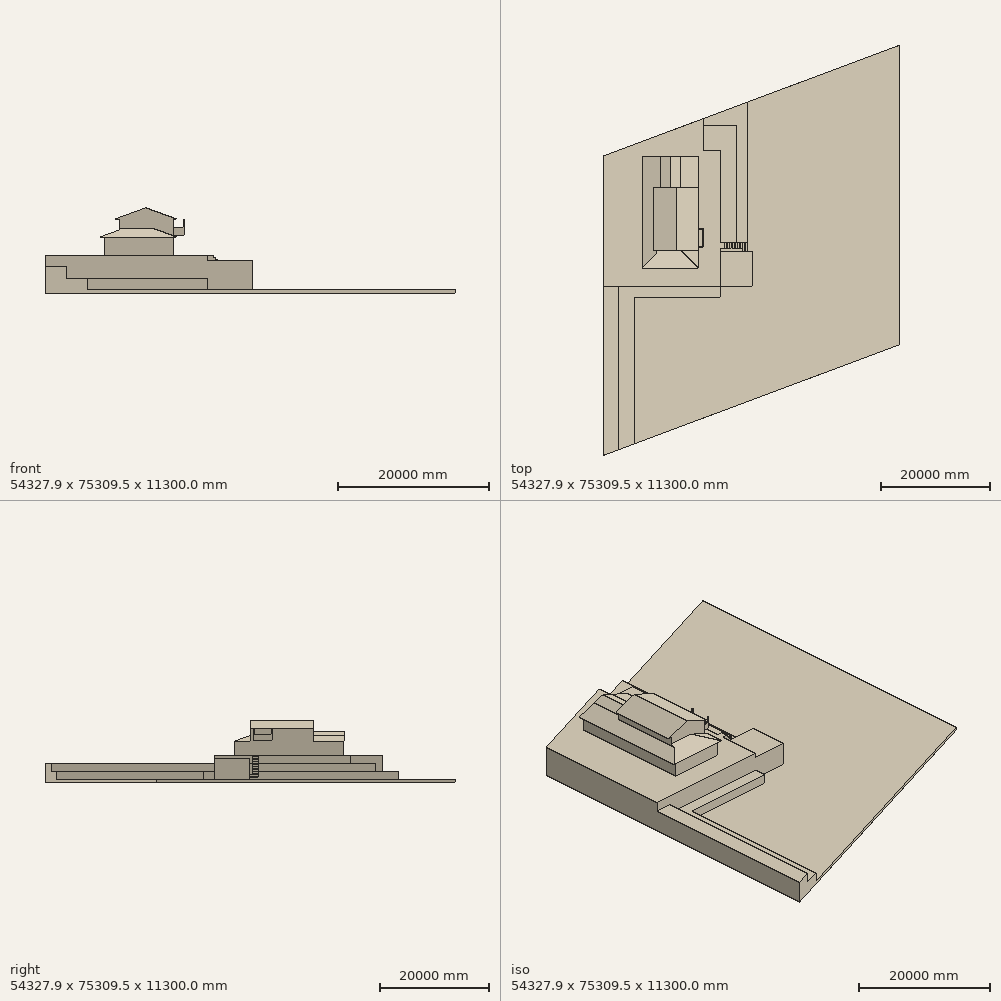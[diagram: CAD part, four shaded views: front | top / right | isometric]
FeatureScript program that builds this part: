
annotation { "Feature Type Name" : "Feature", "Feature Type Description" : "" }
export const myFeature = defineFeature(function(context is Context, id is Id, definition is map)
    precondition{}
    {
        {
            var Q0;
            Q0=qCreatedBy(makeId("Top.planeOp"),FACE);
            var sketch = newSketch(context, id + "F0", { "sketchPlane" : qUnion([Q0])});
            skLineSegment(sketch, "E0.bottom", {"start": v(0, 0) * mm, "end": v(-9140, 0) * mm});
            skLineSegment(sketch, "E0.top", {"start": v(0, 20000) * mm, "end": v(-9140, 20000) * mm});
            skLineSegment(sketch, "E0.left", {"start": v(0, 0) * mm, "end": v(0, 20000) * mm});
            skLineSegment(sketch, "E0.right", {"start": v(-9140, 0) * mm, "end": v(-9140, 20000) * mm});
            skSolve(sketch);
        }
        {
            var Q0;
            Q0=qSketchRegion(id+"F0",true);
            extrude(context, id + "F1", {"entities" : qUnion([Q0]), "depth" : 2400 * mm, "offsetDistance" : 25 * mm});
        }
        {
            var Q0;
            Q0=makeQuery(id+"F1.opExtrude","CAP_FACE",FACE,{"disambiguationData":[OSD([sQuery(id+"F0.wireOp",EDGE,"E0.bottom"),sQuery(id+"F0.wireOp",EDGE,"E0.top"),sQuery(id+"F0.wireOp",EDGE,"E0.left"),sQuery(id+"F0.wireOp",EDGE,"E0.right")])],"isStart":false});
            var sketch = newSketch(context, id + "F2", { "sketchPlane" : qUnion([Q0])});
            skLineSegment(sketch, "E1", {"start": v(0, 0) * mm, "end": v(0, 3000) * mm});
            skLineSegment(sketch, "E2", {"start": v(0, 3000) * mm, "end": v(-7140, 3000) * mm});
            skLineSegment(sketch, "E3", {"start": v(-7140, 3000) * mm, "end": v(-7140, 14500) * mm});
            skLineSegment(sketch, "E4", {"start": v(-7140, 14500) * mm, "end": v(0, 14500) * mm});
            skLineSegment(sketch, "E5", {"start": v(0, 14500) * mm, "end": v(0, 3000) * mm});
            skSolve(sketch);
        }
        {
            var Q0;
            Q0=qSketchRegion(id+"F2",true);
            extrude(context, id + "F3", {"entities" : qUnion([Q0]), "operationType" : NewBodyOperationType.ADD, "depth" : 2400 * mm, "offsetDistance" : 25 * mm});
        }
        {
            var Q0;
            Q0=makeQuery(id+"F3.opExtrude","CAP_FACE",FACE,{"disambiguationData":[OSD([sQuery(id+"F2.wireOp",EDGE,"E2"),sQuery(id+"F2.wireOp",EDGE,"E3"),sQuery(id+"F2.wireOp",EDGE,"E4"),sQuery(id+"F2.wireOp",EDGE,"E5")])],"isStart":false});
            var sketch = newSketch(context, id + "F4", { "sketchPlane" : qUnion([Q0])});
            skLineSegment(sketch, "E6", {"start": v(-3570, 3000) * mm, "end": v(-7740, 3000) * mm});
            skLineSegment(sketch, "E7", {"start": v(-7740, 3000) * mm, "end": v(-7740, 14500) * mm});
            skLineSegment(sketch, "E8", {"start": v(-7740, 14500) * mm, "end": v(600, 14500) * mm});
            skLineSegment(sketch, "E9", {"start": v(600, 14500) * mm, "end": v(600, 3000) * mm});
            skLineSegment(sketch, "E10", {"start": v(600, 3000) * mm, "end": v(-3570, 3000) * mm});
            skSolve(sketch);
        }
        {
            var Q0;
            Q0=qSketchRegion(id+"F4",true);
            extrude(context, id + "F5", {"entities" : qUnion([Q0]), "operationType" : NewBodyOperationType.ADD, "depth" : 1500 * mm, "offsetDistance" : 25 * mm});
        }
        {
            var Q0;
            Q0=makeQuery(id+"F5.opExtrude","CAP_EDGE",EDGE,{"disambiguationData":[OSD([sQuery(id+"F4.wireOp",EDGE,"E9")])],"isStart":false});
            var Q1;
            Q1=makeQuery(id+"F5.opExtrude","CAP_EDGE",EDGE,{"disambiguationData":[OSD([sQuery(id+"F4.wireOp",EDGE,"E7")])],"isStart":false});
            chamfer(context, id + "F6", {"entities" : qUnion([Q0, Q1]), "chamferType" : ChamferType.OFFSET_ANGLE, "width" : 4170 * mm, "oppositeDirection" : true, "angle" : 20 * degree, "tangentPropagation" : true});
        }
        {
            var Q0;
            Q0=makeQuery(id+"F1.opExtrude","CAP_FACE",FACE,{"disambiguationData":[OSD([sQuery(id+"F0.wireOp",EDGE,"E0.bottom"),sQuery(id+"F0.wireOp",EDGE,"E0.top"),sQuery(id+"F0.wireOp",EDGE,"E0.left"),sQuery(id+"F0.wireOp",EDGE,"E0.right")])],"isStart":false});
            var sketch = newSketch(context, id + "F7", { "sketchPlane" : qUnion([Q0])});
            skLineSegment(sketch, "E11", {"start": v(0, 3000) * mm, "end": v(-7140, 3000) * mm});
            skLineSegment(sketch, "E12", {"start": v(-9740, 3000) * mm, "end": v(-9740, -300) * mm});
            skLineSegment(sketch, "E13", {"start": v(-9740, -300) * mm, "end": v(600, -300) * mm});
            skLineSegment(sketch, "E14", {"start": v(600, -300) * mm, "end": v(600, 3000) * mm});
            skLineSegment(sketch, "E15", {"start": v(600, 3000) * mm, "end": v(0, 3000) * mm});
            skPoint(sketch, "E16.start.orphan", {"position": v(600, 14500) * mm});
            skLineSegment(sketch, "E17", {"start": v(-7140, 3000) * mm, "end": v(-7140, 14500) * mm});
            skLineSegment(sketch, "E18", {"start": v(-7140, 14500) * mm, "end": v(600, 14500) * mm});
            skLineSegment(sketch, "E19", {"start": v(600, 14500) * mm, "end": v(600, 20300) * mm});
            skLineSegment(sketch, "E20", {"start": v(600, 20300) * mm, "end": v(-9740, 20300) * mm});
            skLineSegment(sketch, "E21", {"start": v(-9740, 20300) * mm, "end": v(-9740, 3000) * mm});
            skSolve(sketch);
        }
        {
            var Q0;
            Q0=qSketchRegion(id+"F7",true);
            extrude(context, id + "F8", {"entities" : qUnion([Q0]), "operationType" : NewBodyOperationType.ADD, "depth" : 1200 * mm, "offsetDistance" : 25 * mm});
        }
        {
            var Q0;
            Q0=makeQuery(id+"F8.opExtrude","CAP_EDGE",EDGE,{"disambiguationData":[OSD([sQuery(id+"F7.wireOp",EDGE,"E13")])],"isStart":false});
            var Q1;
            Q1=makeQuery(id+"F8.opExtrude","CAP_EDGE",EDGE,{"disambiguationData":[OSD([sQuery(id+"F7.wireOp",EDGE,"E14")])],"isStart":false});
            chamfer(context, id + "F9", {"entities" : qUnion([Q0, Q1]), "chamferType" : ChamferType.OFFSET_ANGLE, "width" : 3300 * mm, "oppositeDirection" : false, "angle" : 20 * degree, "tangentPropagation" : true});
        }
        {
            var Q0;
            Q0=makeQuery(id+"F8.opExtrude","CAP_EDGE",EDGE,{"disambiguationData":[OSD([sQuery(id+"F7.wireOp",EDGE,"E19")])],"isStart":false});
            var Q1;
            Q1=makeQuery(id+"F8.opExtrude","CAP_EDGE",EDGE,{"disambiguationData":[OSD([sQuery(id+"F7.wireOp",EDGE,"E12"),sQuery(id+"F7.wireOp",EDGE,"E21")])],"isStart":false});
            chamfer(context, id + "F10", {"entities" : qUnion([Q0, Q1]), "chamferType" : ChamferType.OFFSET_ANGLE, "width" : 3300 * mm, "oppositeDirection" : false, "angle" : 20 * degree, "tangentPropagation" : true});
        }
        {
            var Q0;
            Q0=makeQuery(id+"F8.opExtrude","CAP_FACE",FACE,{"disambiguationData":[OSD([sQuery(id+"F7.wireOp",EDGE,"E11"),sQuery(id+"F7.wireOp",EDGE,"E12"),sQuery(id+"F7.wireOp",EDGE,"E13"),sQuery(id+"F7.wireOp",EDGE,"E14"),sQuery(id+"F7.wireOp",EDGE,"E15"),sQuery(id+"F7.wireOp",EDGE,"E17"),sQuery(id+"F7.wireOp",EDGE,"E18"),sQuery(id+"F7.wireOp",EDGE,"E19"),sQuery(id+"F7.wireOp",EDGE,"E20"),sQuery(id+"F7.wireOp",EDGE,"E21")])],"isStart":false});
            extrude(context, id + "F11", {"entities" : qUnion([Q0]), "operationType" : NewBodyOperationType.ADD, "depth" : 700 * mm, "offsetDistance" : 25 * mm});
        }
        {
            var Q0;
            {var subQ0=sQuery(id+"F7.wireOp",EDGE,"E21");var subQ1=sQuery(id+"F7.wireOp",EDGE,"E20");var subQ2=sQuery(id+"F7.wireOp",EDGE,"E19");var subQ3=sQuery(id+"F7.wireOp",EDGE,"E18");var subQ4=sQuery(id+"F7.wireOp",EDGE,"E17");var subQ5=sQuery(id+"F7.wireOp",EDGE,"E15");var subQ6=sQuery(id+"F7.wireOp",EDGE,"E14");var subQ7=sQuery(id+"F7.wireOp",EDGE,"E13");var subQ8=sQuery(id+"F7.wireOp",EDGE,"E12");var subQ9=sQuery(id+"F7.wireOp",EDGE,"E11");Q0=makeQuery(id+"F11.opExtrude","CAP_EDGE",EDGE,{"disambiguationData":[OSD([subQ9,subQ8,subQ7,subQ6,subQ5,subQ4,subQ3,subQ2,subQ1,subQ0]),TDD([makeQuery(id+"F10.opChamfer","BLEND_EDGE",EDGE,{"blendedFrom":[makeQuery(id+"F8.opExtrude","CAP_EDGE",EDGE,{"disambiguationData":[OSD([subQ8,subQ0])],"isStart":false}),makeQuery(id+"F8.opExtrude","CAP_FACE",FACE,{"disambiguationData":[OSD([subQ9,subQ8,subQ7,subQ6,subQ5,subQ4,subQ3,subQ2,subQ1,subQ0])],"isStart":false})],"blendedInto":[makeQuery(id+"F8.opExtrude","CAP_FACE",FACE,{"disambiguationData":[OSD([subQ9,subQ8,subQ7,subQ6,subQ5,subQ4,subQ3,subQ2,subQ1,subQ0])],"isStart":false})]})])],"isStart":false});}
            var Q1;
            {var subQ0=sQuery(id+"F7.wireOp",EDGE,"E21");var subQ1=sQuery(id+"F7.wireOp",EDGE,"E20");var subQ2=sQuery(id+"F7.wireOp",EDGE,"E19");var subQ3=sQuery(id+"F7.wireOp",EDGE,"E18");var subQ4=sQuery(id+"F7.wireOp",EDGE,"E17");var subQ5=sQuery(id+"F7.wireOp",EDGE,"E15");var subQ6=sQuery(id+"F7.wireOp",EDGE,"E14");var subQ7=sQuery(id+"F7.wireOp",EDGE,"E13");var subQ8=sQuery(id+"F7.wireOp",EDGE,"E12");var subQ9=sQuery(id+"F7.wireOp",EDGE,"E11");Q1=makeQuery(id+"F11.opExtrude","CAP_EDGE",EDGE,{"disambiguationData":[OSD([subQ9,subQ8,subQ7,subQ6,subQ5,subQ4,subQ3,subQ2,subQ1,subQ0]),TDD([makeQuery(id+"F10.opChamfer","BLEND_EDGE",EDGE,{"blendedFrom":[makeQuery(id+"F8.opExtrude","CAP_EDGE",EDGE,{"disambiguationData":[OSD([subQ2])],"isStart":false}),makeQuery(id+"F8.opExtrude","CAP_FACE",FACE,{"disambiguationData":[OSD([subQ9,subQ8,subQ7,subQ6,subQ5,subQ4,subQ3,subQ2,subQ1,subQ0])],"isStart":false})],"blendedInto":[makeQuery(id+"F8.opExtrude","CAP_FACE",FACE,{"disambiguationData":[OSD([subQ9,subQ8,subQ7,subQ6,subQ5,subQ4,subQ3,subQ2,subQ1,subQ0])],"isStart":false})]})])],"isStart":false});}
            chamfer(context, id + "F12", {"entities" : qUnion([Q0, Q1]), "chamferType" : ChamferType.OFFSET_ANGLE, "width" : 1923.2 * mm, "oppositeDirection" : false, "angle" : 20 * degree, "tangentPropagation" : true});
        }
        {
            var Q0;
            Q0=makeQuery(id+"F1.opExtrude","CAP_FACE",FACE,{"disambiguationData":[OSD([sQuery(id+"F0.wireOp",EDGE,"E0.bottom"),sQuery(id+"F0.wireOp",EDGE,"E0.top"),sQuery(id+"F0.wireOp",EDGE,"E0.left"),sQuery(id+"F0.wireOp",EDGE,"E0.right")])],"isStart":true});
            var sketch = newSketch(context, id + "F13", { "sketchPlane" : qUnion([Q0])});
            skLineSegment(sketch, "E22", {"start": v(0, 0) * mm, "end": v(0, 3700) * mm});
            skLineSegment(sketch, "E23", {"start": v(0, 3700) * mm, "end": v(4500, 3700) * mm});
            skLineSegment(sketch, "E24", {"start": v(4500, 3700) * mm, "end": v(4500, -28300) * mm});
            skLineSegment(sketch, "E25", {"start": v(0, 3700) * mm, "end": v(-16900, 3700) * mm});
            skLineSegment(sketch, "E26", {"start": v(-16900, 3700) * mm, "end": v(-16900, -20300) * mm});
            skLineSegment(sketch, "E27", {"start": v(-16900, -20300) * mm, "end": v(4500, -28300) * mm});
            skSolve(sketch);
        }
        {
            var Q0;
            Q0=qSketchRegion(id+"F13",true);
            extrude(context, id + "F14", {"entities" : qUnion([Q0]), "operationType" : NewBodyOperationType.ADD, "depth" : 200 * mm, "offsetDistance" : 25 * mm});
        }
        {
            var Q0;
            Q0=makeQuery(id+"F14.opExtrude","CAP_FACE",FACE,{"disambiguationData":[OSD([sQuery(id+"F13.wireOp",EDGE,"E23"),sQuery(id+"F13.wireOp",EDGE,"E24"),sQuery(id+"F13.wireOp",EDGE,"E25"),sQuery(id+"F13.wireOp",EDGE,"E26"),sQuery(id+"F13.wireOp",EDGE,"E27")])],"isStart":false});
            var sketch = newSketch(context, id + "F15", { "sketchPlane" : qUnion([Q0])});
            skLineSegment(sketch, "E28", {"start": v(-16900, -20300) * mm, "end": v(37427.93, -40609.5) * mm});
            skLineSegment(sketch, "E29", {"start": v(37427.93, -40609.5) * mm, "end": v(37427.93, 14390.5) * mm});
            skLineSegment(sketch, "E30", {"start": v(37427.93, 14390.5) * mm, "end": v(-16900, 34700) * mm});
            skLineSegment(sketch, "E31", {"start": v(-16900, 34700) * mm, "end": v(-16900, -20300) * mm});
            skSolve(sketch);
        }
        {
            var Q0;
            Q0=qSketchRegion(id+"F15",true);
            extrude(context, id + "F16", {"entities" : qUnion([Q0]), "operationType" : NewBodyOperationType.ADD, "depth" : 4800 * mm, "offsetDistance" : 25 * mm});
        }
        {
            var Q0;
            Q0=makeQuery(id+"F16.opExtrude","CAP_FACE",FACE,{"disambiguationData":[OSD([sQuery(id+"F15.wireOp",EDGE,"E28"),sQuery(id+"F15.wireOp",EDGE,"E29"),sQuery(id+"F15.wireOp",EDGE,"E30"),sQuery(id+"F15.wireOp",EDGE,"E31")])],"isStart":true});
            extrude(context, id + "F17", {"entities" : qUnion([Q0]), "operationType" : NewBodyOperationType.ADD, "depth" : 25 * mm, "offsetDistance" : 25 * mm});
        }
        {
            var Q0;
            Q0=makeQuery(id+"F17.opExtrude","CAP_FACE",FACE,{"disambiguationData":[OSD([sQuery(id+"F15.wireOp",EDGE,"E28"),sQuery(id+"F15.wireOp",EDGE,"E29"),sQuery(id+"F15.wireOp",EDGE,"E30"),sQuery(id+"F15.wireOp",EDGE,"E31")])],"isStart":false});
            var sketch = newSketch(context, id + "F18", { "sketchPlane" : qUnion([Q0])});
            skLineSegment(sketch, "E32", {"start": v(-16900, -3700) * mm, "end": v(4500, -3700) * mm});
            skLineSegment(sketch, "E33", {"start": v(4500, -3700) * mm, "end": v(4500, 28300) * mm});
            skLineSegment(sketch, "E34", {"start": v(4500, 28300) * mm, "end": v(37427.93, 40609.5) * mm});
            skLineSegment(sketch, "E35", {"start": v(37427.93, 40609.5) * mm, "end": v(37427.93, -14390.5) * mm});
            skLineSegment(sketch, "E36", {"start": v(37427.93, -14390.5) * mm, "end": v(-16900, -34700) * mm});
            skLineSegment(sketch, "E37", {"start": v(-16900, -34700) * mm, "end": v(-16900, -3700) * mm});
            skSolve(sketch);
        }
        {
            var Q0;
            Q0=qSketchRegion(id+"F18",true);
            extrude(context, id + "F19", {"entities" : qUnion([Q0]), "operationType" : NewBodyOperationType.REMOVE, "oppositeDirection" : true, "depth" : 1325 * mm, "offsetDistance" : 25 * mm});
        }
        {
            var Q0;
            Q0=makeQuery(id+"F14.opExtrude","CAP_FACE",FACE,{"disambiguationData":[OSD([sQuery(id+"F13.wireOp",EDGE,"E23"),sQuery(id+"F13.wireOp",EDGE,"E24"),sQuery(id+"F13.wireOp",EDGE,"E25"),sQuery(id+"F13.wireOp",EDGE,"E26"),sQuery(id+"F13.wireOp",EDGE,"E27")])],"isStart":true});
            var sketch = newSketch(context, id + "F20", { "sketchPlane" : qUnion([Q0])});
            skLineSegment(sketch, "E38", {"start": v(4500, 28300) * mm, "end": v(4500, 21300) * mm});
            skLineSegment(sketch, "E39", {"start": v(4500, 21300) * mm, "end": v(1500, 21300) * mm});
            skLineSegment(sketch, "E40", {"start": v(1500, 21300) * mm, "end": v(1500, 27178.5) * mm});
            skLineSegment(sketch, "E41", {"start": v(1500, 27178.5) * mm, "end": v(4500, 28300) * mm});
            skSolve(sketch);
        }
        {
            var Q0;
            Q0=qSketchRegion(id+"F20",true);
            extrude(context, id + "F21", {"entities" : qUnion([Q0]), "operationType" : NewBodyOperationType.REMOVE, "oppositeDirection" : true, "depth" : 1500 * mm, "offsetDistance" : 25 * mm});
        }
        {
            var Q0;
            Q0=makeQuery(id+"F21.boolean.opBoolean","MERGE",FACE,{"derivedFrom":[makeQuery(id+"F19.boolean.opBoolean","COPY",FACE,{"derivedFrom":makeQuery(id+"F19.opExtrude","CAP_FACE",FACE,{"disambiguationData":[OSD([sQuery(id+"F18.wireOp",EDGE,"E32"),sQuery(id+"F18.wireOp",EDGE,"E33"),sQuery(id+"F18.wireOp",EDGE,"E34"),sQuery(id+"F18.wireOp",EDGE,"E35"),sQuery(id+"F18.wireOp",EDGE,"E36"),sQuery(id+"F18.wireOp",EDGE,"E37")])],"isStart":false})})],"fromTools":[makeQuery(id+"F21.opExtrude","CAP_FACE",FACE,{"disambiguationData":[OSD([sQuery(id+"F20.wireOp",EDGE,"E38"),sQuery(id+"F20.wireOp",EDGE,"E39"),sQuery(id+"F20.wireOp",EDGE,"E40"),sQuery(id+"F20.wireOp",EDGE,"E41")])],"isStart":false})]});
            var sketch = newSketch(context, id + "F22", { "sketchPlane" : qUnion([Q0])});
            skLineSegment(sketch, "E42", {"start": v(4500, -3700) * mm, "end": v(4500, 4440) * mm});
            skLineSegment(sketch, "E43", {"start": v(4500, 4440) * mm, "end": v(7500, 4440) * mm});
            skLineSegment(sketch, "E44", {"start": v(7500, 4440) * mm, "end": v(7500, 25900) * mm});
            skLineSegment(sketch, "E45", {"start": v(7500, 25900) * mm, "end": v(1500, 25900) * mm});
            skLineSegment(sketch, "E46", {"start": v(1500, 25900) * mm, "end": v(1500, 27178.5) * mm});
            skLineSegment(sketch, "E47", {"start": v(1500, 27178.5) * mm, "end": v(37427.93, 40609.5) * mm});
            skLineSegment(sketch, "E48", {"start": v(37427.93, 40609.5) * mm, "end": v(37427.93, -14390.5) * mm});
            skLineSegment(sketch, "E49", {"start": v(37427.93, -14390.5) * mm, "end": v(-14089.93, -33649.5) * mm});
            skLineSegment(sketch, "E50", {"start": v(-14089.93, -33649.5) * mm, "end": v(-14089.93, -3700) * mm});
            skLineSegment(sketch, "E51", {"start": v(-14089.93, -3700) * mm, "end": v(4500, -3700) * mm});
            skSolve(sketch);
        }
        {
            var Q0;
            Q0=qSketchRegion(id+"F22",true);
            extrude(context, id + "F23", {"entities" : qUnion([Q0]), "operationType" : NewBodyOperationType.REMOVE, "oppositeDirection" : true, "depth" : 1500 * mm, "offsetDistance" : 25 * mm});
        }
        {
            var Q0;
            Q0=makeQuery(id+"F23.boolean.opBoolean","COPY",FACE,{"derivedFrom":makeQuery(id+"F23.opExtrude","CAP_FACE",FACE,{"disambiguationData":[OSD([sQuery(id+"F22.wireOp",EDGE,"E42"),sQuery(id+"F22.wireOp",EDGE,"E43"),sQuery(id+"F22.wireOp",EDGE,"E44"),sQuery(id+"F22.wireOp",EDGE,"E45"),sQuery(id+"F22.wireOp",EDGE,"E46"),sQuery(id+"F22.wireOp",EDGE,"E47"),sQuery(id+"F22.wireOp",EDGE,"E48"),sQuery(id+"F22.wireOp",EDGE,"E49"),sQuery(id+"F22.wireOp",EDGE,"E50"),sQuery(id+"F22.wireOp",EDGE,"E51")])],"isStart":false})});
            var sketch = newSketch(context, id + "F24", { "sketchPlane" : qUnion([Q0])});
            skLineSegment(sketch, "E52", {"start": v(4500, -3700) * mm, "end": v(4500, 4440) * mm});
            skLineSegment(sketch, "E53", {"start": v(4500, 4440) * mm, "end": v(9500, 4440) * mm});
            skLineSegment(sketch, "E54", {"start": v(9500, 4440) * mm, "end": v(9500, 30169.16) * mm});
            skLineSegment(sketch, "E55", {"start": v(9500, 30169.16) * mm, "end": v(37427.93, 40609.5) * mm});
            skLineSegment(sketch, "E56", {"start": v(37427.93, 40609.5) * mm, "end": v(37427.93, -14390.5) * mm});
            skLineSegment(sketch, "E57", {"start": v(37427.93, -14390.5) * mm, "end": v(-11279.87, -32599.02) * mm});
            skLineSegment(sketch, "E58", {"start": v(-11279.87, -32599.02) * mm, "end": v(-11279.87, -5700) * mm});
            skLineSegment(sketch, "E59", {"start": v(-11279.87, -5700) * mm, "end": v(4500, -5700) * mm});
            skLineSegment(sketch, "E60", {"start": v(4500, -5700) * mm, "end": v(4500, -3700) * mm});
            skSolve(sketch);
        }
        {
            var Q0;
            Q0=qSketchRegion(id+"F24",true);
            extrude(context, id + "F25", {"entities" : qUnion([Q0]), "operationType" : NewBodyOperationType.REMOVE, "oppositeDirection" : true, "depth" : 1500 * mm, "offsetDistance" : 25 * mm});
        }
        {
            var Q0;
            Q0=makeQuery(id+"F25.boolean.opBoolean","COPY",FACE,{"derivedFrom":makeQuery(id+"F25.opExtrude","CAP_FACE",FACE,{"disambiguationData":[OSD([sQuery(id+"F24.wireOp",EDGE,"E52"),sQuery(id+"F24.wireOp",EDGE,"E53"),sQuery(id+"F24.wireOp",EDGE,"E54"),sQuery(id+"F24.wireOp",EDGE,"E55"),sQuery(id+"F24.wireOp",EDGE,"E56"),sQuery(id+"F24.wireOp",EDGE,"E57"),sQuery(id+"F24.wireOp",EDGE,"E58"),sQuery(id+"F24.wireOp",EDGE,"E59"),sQuery(id+"F24.wireOp",EDGE,"E60")])],"isStart":false})});
            var sketch = newSketch(context, id + "F26", { "sketchPlane" : qUnion([Q0])});
            skLineSegment(sketch, "E61", {"start": v(4500, -3700) * mm, "end": v(4500, 3300) * mm});
            skLineSegment(sketch, "E62", {"start": v(4500, 3300) * mm, "end": v(10500, 3300) * mm});
            skLineSegment(sketch, "E63", {"start": v(10500, 3300) * mm, "end": v(10500, -3700) * mm});
            skLineSegment(sketch, "E64", {"start": v(10500, -3700) * mm, "end": v(4500, -3700) * mm});
            skSolve(sketch);
        }
        {
            var Q0;
            Q0=qSketchRegion(id+"F26",true);
            extrude(context, id + "F27", {"entities" : qUnion([Q0]), "operationType" : NewBodyOperationType.ADD, "depth" : 3800 * mm, "offsetDistance" : 25 * mm});
        }
        {
            var Q0;
            Q0=makeQuery(id+"F25.boolean.opBoolean","COPY",FACE,{"derivedFrom":makeQuery(id+"F25.opExtrude","CAP_FACE",FACE,{"disambiguationData":[OSD([sQuery(id+"F24.wireOp",EDGE,"E52"),sQuery(id+"F24.wireOp",EDGE,"E53"),sQuery(id+"F24.wireOp",EDGE,"E54"),sQuery(id+"F24.wireOp",EDGE,"E55"),sQuery(id+"F24.wireOp",EDGE,"E56"),sQuery(id+"F24.wireOp",EDGE,"E57"),sQuery(id+"F24.wireOp",EDGE,"E58"),sQuery(id+"F24.wireOp",EDGE,"E59"),sQuery(id+"F24.wireOp",EDGE,"E60")])],"isStart":false})});
            var sketch = newSketch(context, id + "F28", { "sketchPlane" : qUnion([Q0])});
            skLineSegment(sketch, "E65", {"start": v(9500, 4440) * mm, "end": v(9500, 3300) * mm});
            skLineSegment(sketch, "E66", {"start": v(9500, 3300) * mm, "end": v(4500, 3300) * mm});
            skLineSegment(sketch, "E67", {"start": v(4500, 3300) * mm, "end": v(4500, 4440) * mm});
            skLineSegment(sketch, "E68", {"start": v(4500, 4440) * mm, "end": v(9500, 4440) * mm});
            skSolve(sketch);
        }
        {
            var Q0;
            Q0=qSketchRegion(id+"F28",true);
            extrude(context, id + "F29", {"entities" : qUnion([Q0]), "operationType" : NewBodyOperationType.ADD, "depth" : 300 * mm, "offsetDistance" : 25 * mm});
        }
        {
            var Q0;
            Q0=makeQuery(id+"F29.opExtrude","CAP_FACE",FACE,{"disambiguationData":[OSD([sQuery(id+"F28.wireOp",EDGE,"E65"),sQuery(id+"F28.wireOp",EDGE,"E66"),sQuery(id+"F28.wireOp",EDGE,"E67"),sQuery(id+"F28.wireOp",EDGE,"E68")])],"isStart":false});
            var sketch = newSketch(context, id + "F30", { "sketchPlane" : qUnion([Q0])});
            skLineSegment(sketch, "E69", {"start": v(4500, 4440) * mm, "end": v(9200, 4440) * mm});
            skLineSegment(sketch, "E70", {"start": v(9200, 4440) * mm, "end": v(9200, 3300) * mm});
            skLineSegment(sketch, "E71", {"start": v(9200, 3300) * mm, "end": v(4500, 3300) * mm});
            skLineSegment(sketch, "E72", {"start": v(4500, 3300) * mm, "end": v(4500, 4351.93) * mm});
            skLineSegment(sketch, "E73", {"start": v(4500, 4351.93) * mm, "end": v(4500, 4440) * mm});
            skSolve(sketch);
        }
        {
            var Q0;
            Q0=qSketchRegion(id+"F30",true);
            extrude(context, id + "F31", {"entities" : qUnion([Q0]), "operationType" : NewBodyOperationType.ADD, "depth" : 300 * mm, "offsetDistance" : 25 * mm});
        }
        {
            var Q0;
            Q0=makeQuery(id+"F31.opExtrude","CAP_FACE",FACE,{"disambiguationData":[OSD([sQuery(id+"F30.wireOp",EDGE,"E69"),sQuery(id+"F30.wireOp",EDGE,"E70"),sQuery(id+"F30.wireOp",EDGE,"E71"),sQuery(id+"F30.wireOp",EDGE,"E72"),sQuery(id+"F30.wireOp",EDGE,"E73")])],"isStart":false});
            var sketch = newSketch(context, id + "F32", { "sketchPlane" : qUnion([Q0])});
            skLineSegment(sketch, "E74.bottom", {"start": v(4500, 4440) * mm, "end": v(8900, 4440) * mm});
            skLineSegment(sketch, "E74.top", {"start": v(4500, 3300) * mm, "end": v(8900, 3300) * mm});
            skLineSegment(sketch, "E74.left", {"start": v(4500, 4440) * mm, "end": v(4500, 3300) * mm});
            skLineSegment(sketch, "E74.right", {"start": v(8900, 4440) * mm, "end": v(8900, 3300) * mm});
            skSolve(sketch);
        }
        {
            var Q0;
            Q0=qSketchRegion(id+"F32",true);
            extrude(context, id + "F33", {"entities" : qUnion([Q0]), "operationType" : NewBodyOperationType.ADD, "depth" : 300 * mm, "offsetDistance" : 25 * mm});
        }
        {
            var Q0;
            Q0=makeQuery(id+"F33.opExtrude","CAP_FACE",FACE,{"disambiguationData":[OSD([sQuery(id+"F32.wireOp",EDGE,"E74.bottom"),sQuery(id+"F32.wireOp",EDGE,"E74.top"),sQuery(id+"F32.wireOp",EDGE,"E74.left"),sQuery(id+"F32.wireOp",EDGE,"E74.right")])],"isStart":false});
            var sketch = newSketch(context, id + "F34", { "sketchPlane" : qUnion([Q0])});
            skLineSegment(sketch, "E75.bottom", {"start": v(4500, 4440) * mm, "end": v(8600, 4440) * mm});
            skLineSegment(sketch, "E75.top", {"start": v(4500, 3300) * mm, "end": v(8600, 3300) * mm});
            skLineSegment(sketch, "E75.left", {"start": v(4500, 4440) * mm, "end": v(4500, 3300) * mm});
            skLineSegment(sketch, "E75.right", {"start": v(8600, 4440) * mm, "end": v(8600, 3300) * mm});
            skSolve(sketch);
        }
        {
            var Q0;
            Q0=qSketchRegion(id+"F34",true);
            extrude(context, id + "F35", {"entities" : qUnion([Q0]), "operationType" : NewBodyOperationType.ADD, "depth" : 300 * mm, "offsetDistance" : 25 * mm});
        }
        {
            var Q0;
            Q0=makeQuery(id+"F35.opExtrude","CAP_FACE",FACE,{"disambiguationData":[OSD([sQuery(id+"F34.wireOp",EDGE,"E75.bottom"),sQuery(id+"F34.wireOp",EDGE,"E75.top"),sQuery(id+"F34.wireOp",EDGE,"E75.left"),sQuery(id+"F34.wireOp",EDGE,"E75.right")])],"isStart":false});
            var sketch = newSketch(context, id + "F36", { "sketchPlane" : qUnion([Q0])});
            skLineSegment(sketch, "E76.bottom", {"start": v(4500, 4440) * mm, "end": v(8300, 4440) * mm});
            skLineSegment(sketch, "E76.top", {"start": v(4500, 3300) * mm, "end": v(8300, 3300) * mm});
            skLineSegment(sketch, "E76.left", {"start": v(4500, 4440) * mm, "end": v(4500, 3300) * mm});
            skLineSegment(sketch, "E76.right", {"start": v(8300, 4440) * mm, "end": v(8300, 3300) * mm});
            skSolve(sketch);
        }
        {
            var Q0;
            Q0=qSketchRegion(id+"F36",true);
            extrude(context, id + "F37", {"entities" : qUnion([Q0]), "operationType" : NewBodyOperationType.ADD, "depth" : 300 * mm, "offsetDistance" : 25 * mm});
        }
        {
            var Q0;
            {var subQ1=sQuery(id+"F22.wireOp",EDGE,"E45");var subQ2=sQuery(id+"F22.wireOp",EDGE,"E43");var subQ3=sQuery(id+"F22.wireOp",EDGE,"E44");Q0=makeQuery(id+"F37.boolean.opBoolean","MERGE",FACE,{"derivedFrom":[makeQuery(id+"F25.boolean.opBoolean","SPLIT",FACE,{"disambiguationData":[TD([makeQuery(id+"F14.opExtrude","SWEPT_FACE",FACE,{"disambiguationData":[OSD([sQuery(id+"F13.wireOp",EDGE,"E27")])]})])],"derivedFrom":makeQuery(id+"F23.boolean.opBoolean","COPY",FACE,{"derivedFrom":makeQuery(id+"F23.opExtrude","CAP_FACE",FACE,{"disambiguationData":[OSD([sQuery(id+"F22.wireOp",EDGE,"E42"),subQ2,subQ3,subQ1,sQuery(id+"F22.wireOp",EDGE,"E46"),sQuery(id+"F22.wireOp",EDGE,"E47"),sQuery(id+"F22.wireOp",EDGE,"E48"),sQuery(id+"F22.wireOp",EDGE,"E49"),sQuery(id+"F22.wireOp",EDGE,"E50"),sQuery(id+"F22.wireOp",EDGE,"E51")])],"isStart":false})})}),makeQuery(id+"F37.opExtrude","CAP_FACE",FACE,{"disambiguationData":[OSD([sQuery(id+"F36.wireOp",EDGE,"E76.bottom"),sQuery(id+"F36.wireOp",EDGE,"E76.top"),sQuery(id+"F36.wireOp",EDGE,"E76.left"),sQuery(id+"F36.wireOp",EDGE,"E76.right")])],"isStart":false})]});}
            var sketch = newSketch(context, id + "F38", { "sketchPlane" : qUnion([Q0])});
            skLineSegment(sketch, "E77.bottom", {"start": v(4500, 4440) * mm, "end": v(8000, 4440) * mm});
            skLineSegment(sketch, "E77.top", {"start": v(4500, 3300) * mm, "end": v(8000, 3300) * mm});
            skLineSegment(sketch, "E77.left", {"start": v(4500, 4440) * mm, "end": v(4500, 3300) * mm});
            skLineSegment(sketch, "E77.right", {"start": v(8000, 4440) * mm, "end": v(8000, 3300) * mm});
            skSolve(sketch);
        }
        {
            var Q0;
            Q0=qSketchRegion(id+"F38",true);
            extrude(context, id + "F39", {"entities" : qUnion([Q0]), "operationType" : NewBodyOperationType.ADD, "depth" : 300 * mm, "offsetDistance" : 25 * mm});
        }
        {
            var Q0;
            Q0=makeQuery(id+"F39.opExtrude","CAP_FACE",FACE,{"disambiguationData":[OSD([sQuery(id+"F38.wireOp",EDGE,"E77.bottom"),sQuery(id+"F38.wireOp",EDGE,"E77.top"),sQuery(id+"F38.wireOp",EDGE,"E77.left"),sQuery(id+"F38.wireOp",EDGE,"E77.right")])],"isStart":false});
            var sketch = newSketch(context, id + "F40", { "sketchPlane" : qUnion([Q0])});
            skLineSegment(sketch, "E78.bottom", {"start": v(4500, 4440) * mm, "end": v(7700, 4440) * mm});
            skLineSegment(sketch, "E78.top", {"start": v(4500, 3300) * mm, "end": v(7700, 3300) * mm});
            skLineSegment(sketch, "E78.left", {"start": v(4500, 4440) * mm, "end": v(4500, 3300) * mm});
            skLineSegment(sketch, "E78.right", {"start": v(7700, 4440) * mm, "end": v(7700, 3300) * mm});
            skSolve(sketch);
        }
        {
            var Q0;
            Q0=qSketchRegion(id+"F40",true);
            extrude(context, id + "F41", {"entities" : qUnion([Q0]), "operationType" : NewBodyOperationType.ADD, "depth" : 300 * mm, "offsetDistance" : 25 * mm});
        }
        {
            var Q0;
            Q0=makeQuery(id+"F41.opExtrude","CAP_FACE",FACE,{"disambiguationData":[OSD([sQuery(id+"F40.wireOp",EDGE,"E78.bottom"),sQuery(id+"F40.wireOp",EDGE,"E78.top"),sQuery(id+"F40.wireOp",EDGE,"E78.left"),sQuery(id+"F40.wireOp",EDGE,"E78.right")])],"isStart":false});
            var sketch = newSketch(context, id + "F42", { "sketchPlane" : qUnion([Q0])});
            skLineSegment(sketch, "E79.bottom", {"start": v(4500, 4440) * mm, "end": v(7400, 4440) * mm});
            skLineSegment(sketch, "E79.top", {"start": v(4500, 3300) * mm, "end": v(7400, 3300) * mm});
            skLineSegment(sketch, "E79.left", {"start": v(4500, 4440) * mm, "end": v(4500, 3300) * mm});
            skLineSegment(sketch, "E79.right", {"start": v(7400, 4440) * mm, "end": v(7400, 3300) * mm});
            skSolve(sketch);
        }
        {
            var Q0;
            Q0=qSketchRegion(id+"F42",true);
            extrude(context, id + "F43", {"entities" : qUnion([Q0]), "operationType" : NewBodyOperationType.ADD, "depth" : 300 * mm, "offsetDistance" : 25 * mm});
        }
        {
            var Q0;
            Q0=makeQuery(id+"F43.opExtrude","CAP_FACE",FACE,{"disambiguationData":[OSD([sQuery(id+"F42.wireOp",EDGE,"E79.bottom"),sQuery(id+"F42.wireOp",EDGE,"E79.top"),sQuery(id+"F42.wireOp",EDGE,"E79.left"),sQuery(id+"F42.wireOp",EDGE,"E79.right")])],"isStart":false});
            var sketch = newSketch(context, id + "F44", { "sketchPlane" : qUnion([Q0])});
            skLineSegment(sketch, "E80.bottom", {"start": v(4500, 4440) * mm, "end": v(7100, 4440) * mm});
            skLineSegment(sketch, "E80.top", {"start": v(4500, 3300) * mm, "end": v(7100, 3300) * mm});
            skLineSegment(sketch, "E80.left", {"start": v(4500, 4440) * mm, "end": v(4500, 3300) * mm});
            skLineSegment(sketch, "E80.right", {"start": v(7100, 4440) * mm, "end": v(7100, 3300) * mm});
            skSolve(sketch);
        }
        {
            var Q0;
            Q0=qSketchRegion(id+"F44",true);
            extrude(context, id + "F45", {"entities" : qUnion([Q0]), "operationType" : NewBodyOperationType.ADD, "depth" : 300 * mm, "offsetDistance" : 25 * mm});
        }
        {
            var Q0;
            Q0=makeQuery(id+"F45.opExtrude","CAP_FACE",FACE,{"disambiguationData":[OSD([sQuery(id+"F44.wireOp",EDGE,"E80.bottom"),sQuery(id+"F44.wireOp",EDGE,"E80.top"),sQuery(id+"F44.wireOp",EDGE,"E80.left"),sQuery(id+"F44.wireOp",EDGE,"E80.right")])],"isStart":false});
            var sketch = newSketch(context, id + "F46", { "sketchPlane" : qUnion([Q0])});
            skLineSegment(sketch, "E81.bottom", {"start": v(4500, 4440) * mm, "end": v(6800, 4440) * mm});
            skLineSegment(sketch, "E81.top", {"start": v(4500, 3300) * mm, "end": v(6800, 3300) * mm});
            skLineSegment(sketch, "E81.left", {"start": v(4500, 4440) * mm, "end": v(4500, 3300) * mm});
            skLineSegment(sketch, "E81.right", {"start": v(6800, 4440) * mm, "end": v(6800, 3300) * mm});
            skSolve(sketch);
        }
        {
            var Q0;
            Q0=qSketchRegion(id+"F46",true);
            extrude(context, id + "F47", {"entities" : qUnion([Q0]), "operationType" : NewBodyOperationType.ADD, "depth" : 300 * mm, "offsetDistance" : 25 * mm});
        }
        {
            var Q0;
            {var subQ0=sQuery(id+"F20.wireOp",EDGE,"E40");var subQ1=sQuery(id+"F20.wireOp",EDGE,"E39");Q0=makeQuery(id+"F47.boolean.opBoolean","MERGE",FACE,{"derivedFrom":[makeQuery(id+"F23.boolean.opBoolean","SPLIT",FACE,{"disambiguationData":[TD([makeQuery(id+"F14.opExtrude","SWEPT_FACE",FACE,{"disambiguationData":[OSD([sQuery(id+"F13.wireOp",EDGE,"E24")])]})])],"derivedFrom":makeQuery(id+"F21.boolean.opBoolean","MERGE",FACE,{"derivedFrom":[makeQuery(id+"F19.boolean.opBoolean","COPY",FACE,{"derivedFrom":makeQuery(id+"F19.opExtrude","CAP_FACE",FACE,{"disambiguationData":[OSD([sQuery(id+"F18.wireOp",EDGE,"E32"),sQuery(id+"F18.wireOp",EDGE,"E33"),sQuery(id+"F18.wireOp",EDGE,"E34"),sQuery(id+"F18.wireOp",EDGE,"E35"),sQuery(id+"F18.wireOp",EDGE,"E36"),sQuery(id+"F18.wireOp",EDGE,"E37")])],"isStart":false})})],"fromTools":[makeQuery(id+"F21.opExtrude","CAP_FACE",FACE,{"disambiguationData":[OSD([sQuery(id+"F20.wireOp",EDGE,"E38"),subQ1,subQ0,sQuery(id+"F20.wireOp",EDGE,"E41")])],"isStart":false})]})}),makeQuery(id+"F47.opExtrude","CAP_FACE",FACE,{"disambiguationData":[OSD([sQuery(id+"F46.wireOp",EDGE,"E81.bottom"),sQuery(id+"F46.wireOp",EDGE,"E81.top"),sQuery(id+"F46.wireOp",EDGE,"E81.left"),sQuery(id+"F46.wireOp",EDGE,"E81.right")])],"isStart":false})]});}
            var sketch = newSketch(context, id + "F48", { "sketchPlane" : qUnion([Q0])});
            skLineSegment(sketch, "E82.bottom", {"start": v(4500, 3300) * mm, "end": v(6500, 3300) * mm});
            skLineSegment(sketch, "E82.top", {"start": v(4500, 4440) * mm, "end": v(6500, 4440) * mm});
            skLineSegment(sketch, "E82.left", {"start": v(4500, 3300) * mm, "end": v(4500, 4440) * mm});
            skLineSegment(sketch, "E82.right", {"start": v(6500, 3300) * mm, "end": v(6500, 4440) * mm});
            skSolve(sketch);
        }
        {
            var Q0;
            Q0=qSketchRegion(id+"F48",true);
            extrude(context, id + "F49", {"entities" : qUnion([Q0]), "operationType" : NewBodyOperationType.ADD, "depth" : 300 * mm, "offsetDistance" : 25 * mm});
        }
        {
            var Q0;
            Q0=makeQuery(id+"F49.opExtrude","CAP_FACE",FACE,{"disambiguationData":[OSD([sQuery(id+"F48.wireOp",EDGE,"E82.bottom"),sQuery(id+"F48.wireOp",EDGE,"E82.top"),sQuery(id+"F48.wireOp",EDGE,"E82.left"),sQuery(id+"F48.wireOp",EDGE,"E82.right")])],"isStart":false});
            var sketch = newSketch(context, id + "F50", { "sketchPlane" : qUnion([Q0])});
            skLineSegment(sketch, "E83.bottom", {"start": v(4500, 3300) * mm, "end": v(6200, 3300) * mm});
            skLineSegment(sketch, "E83.top", {"start": v(4500, 4440) * mm, "end": v(6200, 4440) * mm});
            skLineSegment(sketch, "E83.left", {"start": v(4500, 3300) * mm, "end": v(4500, 4440) * mm});
            skLineSegment(sketch, "E83.right", {"start": v(6200, 3300) * mm, "end": v(6200, 4440) * mm});
            skSolve(sketch);
        }
        {
            var Q0;
            Q0=qSketchRegion(id+"F50",true);
            extrude(context, id + "F51", {"entities" : qUnion([Q0]), "operationType" : NewBodyOperationType.ADD, "depth" : 300 * mm, "offsetDistance" : 25 * mm});
        }
        {
            var Q0;
            Q0=makeQuery(id+"F51.opExtrude","CAP_FACE",FACE,{"disambiguationData":[OSD([sQuery(id+"F50.wireOp",EDGE,"E83.bottom"),sQuery(id+"F50.wireOp",EDGE,"E83.top"),sQuery(id+"F50.wireOp",EDGE,"E83.left"),sQuery(id+"F50.wireOp",EDGE,"E83.right")])],"isStart":false});
            var sketch = newSketch(context, id + "F52", { "sketchPlane" : qUnion([Q0])});
            skLineSegment(sketch, "E84.bottom", {"start": v(4500, 3300) * mm, "end": v(5900, 3300) * mm});
            skLineSegment(sketch, "E84.top", {"start": v(4500, 4440) * mm, "end": v(5900, 4440) * mm});
            skLineSegment(sketch, "E84.left", {"start": v(4500, 3300) * mm, "end": v(4500, 4440) * mm});
            skLineSegment(sketch, "E84.right", {"start": v(5900, 3300) * mm, "end": v(5900, 4440) * mm});
            skSolve(sketch);
        }
        {
            var Q0;
            Q0=qSketchRegion(id+"F52",true);
            extrude(context, id + "F53", {"entities" : qUnion([Q0]), "operationType" : NewBodyOperationType.ADD, "depth" : 300 * mm, "offsetDistance" : 25 * mm});
        }
        {
            var Q0;
            Q0=makeQuery(id+"F53.opExtrude","CAP_FACE",FACE,{"disambiguationData":[OSD([sQuery(id+"F52.wireOp",EDGE,"E84.bottom"),sQuery(id+"F52.wireOp",EDGE,"E84.top"),sQuery(id+"F52.wireOp",EDGE,"E84.left"),sQuery(id+"F52.wireOp",EDGE,"E84.right")])],"isStart":false});
            var sketch = newSketch(context, id + "F54", { "sketchPlane" : qUnion([Q0])});
            skLineSegment(sketch, "E85.bottom", {"start": v(4500, 3300) * mm, "end": v(5600, 3300) * mm});
            skLineSegment(sketch, "E85.top", {"start": v(4500, 4440) * mm, "end": v(5600, 4440) * mm});
            skLineSegment(sketch, "E85.left", {"start": v(4500, 3300) * mm, "end": v(4500, 4440) * mm});
            skLineSegment(sketch, "E85.right", {"start": v(5600, 3300) * mm, "end": v(5600, 4440) * mm});
            skSolve(sketch);
        }
        {
            var Q0;
            Q0=qSketchRegion(id+"F54",true);
            extrude(context, id + "F55", {"entities" : qUnion([Q0]), "operationType" : NewBodyOperationType.ADD, "depth" : 300 * mm, "offsetDistance" : 25 * mm});
        }
        {
            var Q0;
            Q0=makeQuery(id+"F55.opExtrude","CAP_FACE",FACE,{"disambiguationData":[OSD([sQuery(id+"F54.wireOp",EDGE,"E85.bottom"),sQuery(id+"F54.wireOp",EDGE,"E85.top"),sQuery(id+"F54.wireOp",EDGE,"E85.left"),sQuery(id+"F54.wireOp",EDGE,"E85.right")])],"isStart":false});
            var sketch = newSketch(context, id + "F56", { "sketchPlane" : qUnion([Q0])});
            skLineSegment(sketch, "E86.bottom", {"start": v(4500, 3300) * mm, "end": v(5300, 3300) * mm});
            skLineSegment(sketch, "E86.top", {"start": v(4500, 4440) * mm, "end": v(5300, 4440) * mm});
            skLineSegment(sketch, "E86.left", {"start": v(4500, 3300) * mm, "end": v(4500, 4440) * mm});
            skLineSegment(sketch, "E86.right", {"start": v(5300, 3300) * mm, "end": v(5300, 4440) * mm});
            skSolve(sketch);
        }
        {
            var Q0;
            Q0=qSketchRegion(id+"F56",true);
            extrude(context, id + "F57", {"entities" : qUnion([Q0]), "operationType" : NewBodyOperationType.ADD, "depth" : 300 * mm, "offsetDistance" : 25 * mm});
        }
        {
            var Q0;
            Q0=makeQuery(id+"F27.opExtrude","CAP_FACE",FACE,{"disambiguationData":[OSD([sQuery(id+"F26.wireOp",EDGE,"E61"),sQuery(id+"F26.wireOp",EDGE,"E62"),sQuery(id+"F26.wireOp",EDGE,"E63"),sQuery(id+"F26.wireOp",EDGE,"E64")])],"isStart":false});
            var sketch = newSketch(context, id + "F58", { "sketchPlane" : qUnion([Q0])});
            skLineSegment(sketch, "E87.bottom", {"start": v(4500, 3300) * mm, "end": v(10500, 3300) * mm});
            skLineSegment(sketch, "E87.top", {"start": v(4500, 2800) * mm, "end": v(10500, 2800) * mm});
            skLineSegment(sketch, "E87.left", {"start": v(4500, 3300) * mm, "end": v(4500, 2800) * mm});
            skLineSegment(sketch, "E87.right", {"start": v(10500, 3300) * mm, "end": v(10500, 2800) * mm});
            skSolve(sketch);
        }
        {
            var Q0;
            Q0=qSketchRegion(id+"F58",true);
            extrude(context, id + "F59", {"entities" : qUnion([Q0]), "operationType" : NewBodyOperationType.REMOVE, "oppositeDirection" : true, "depth" : 800 * mm, "offsetDistance" : 25 * mm});
        }
        {
            var Q0;
            {var subQ0=sQuery(id+"F20.wireOp",EDGE,"E40");var subQ1=sQuery(id+"F20.wireOp",EDGE,"E39");Q0=makeQuery(id+"F59.boolean.opBoolean","MERGE",FACE,{"derivedFrom":[makeQuery(id+"F47.boolean.opBoolean","MERGE",FACE,{"derivedFrom":[makeQuery(id+"F23.boolean.opBoolean","SPLIT",FACE,{"disambiguationData":[TD([makeQuery(id+"F14.opExtrude","SWEPT_FACE",FACE,{"disambiguationData":[OSD([sQuery(id+"F13.wireOp",EDGE,"E24")])]})])],"derivedFrom":makeQuery(id+"F21.boolean.opBoolean","MERGE",FACE,{"derivedFrom":[makeQuery(id+"F19.boolean.opBoolean","COPY",FACE,{"derivedFrom":makeQuery(id+"F19.opExtrude","CAP_FACE",FACE,{"disambiguationData":[OSD([sQuery(id+"F18.wireOp",EDGE,"E32"),sQuery(id+"F18.wireOp",EDGE,"E33"),sQuery(id+"F18.wireOp",EDGE,"E34"),sQuery(id+"F18.wireOp",EDGE,"E35"),sQuery(id+"F18.wireOp",EDGE,"E36"),sQuery(id+"F18.wireOp",EDGE,"E37")])],"isStart":false})})],"fromTools":[makeQuery(id+"F21.opExtrude","CAP_FACE",FACE,{"disambiguationData":[OSD([sQuery(id+"F20.wireOp",EDGE,"E38"),subQ1,subQ0,sQuery(id+"F20.wireOp",EDGE,"E41")])],"isStart":false})]})}),makeQuery(id+"F47.opExtrude","CAP_FACE",FACE,{"disambiguationData":[OSD([sQuery(id+"F46.wireOp",EDGE,"E81.bottom"),sQuery(id+"F46.wireOp",EDGE,"E81.top"),sQuery(id+"F46.wireOp",EDGE,"E81.left"),sQuery(id+"F46.wireOp",EDGE,"E81.right")])],"isStart":false})]})],"fromTools":[makeQuery(id+"F59.opExtrude","CAP_FACE",FACE,{"disambiguationData":[OSD([sQuery(id+"F58.wireOp",EDGE,"E87.bottom"),sQuery(id+"F58.wireOp",EDGE,"E87.top"),sQuery(id+"F58.wireOp",EDGE,"E87.left"),sQuery(id+"F58.wireOp",EDGE,"E87.right")])],"isStart":false})]});}
            var sketch = newSketch(context, id + "F60", { "sketchPlane" : qUnion([Q0])});
            skPoint(sketch, "E88.oppositeSnap0", {"position": v(8650, 3300) * mm});
            skLineSegment(sketch, "E88.bottom", {"start": v(10500, 3300) * mm, "end": v(8650, 3300) * mm});
            skLineSegment(sketch, "E88.top", {"start": v(10500, 2800) * mm, "end": v(8650, 2800) * mm});
            skLineSegment(sketch, "E88.left", {"start": v(10500, 3300) * mm, "end": v(10500, 2800) * mm});
            skLineSegment(sketch, "E88.right", {"start": v(8650, 3300) * mm, "end": v(8650, 2800) * mm});
            skSolve(sketch);
        }
        {
            var Q0;
            Q0=qSketchRegion(id+"F60",true);
            extrude(context, id + "F61", {"entities" : qUnion([Q0]), "operationType" : NewBodyOperationType.REMOVE, "oppositeDirection" : true, "depth" : 2100 * mm, "offsetDistance" : 25 * mm});
        }
        {
            var Q0;
            Q0=makeQuery(id+"F61.boolean.opBoolean","MERGE",FACE,{"derivedFrom":[makeQuery(id+"F33.opExtrude","CAP_FACE",FACE,{"disambiguationData":[OSD([sQuery(id+"F32.wireOp",EDGE,"E74.bottom"),sQuery(id+"F32.wireOp",EDGE,"E74.top"),sQuery(id+"F32.wireOp",EDGE,"E74.left"),sQuery(id+"F32.wireOp",EDGE,"E74.right")])],"isStart":false})],"fromTools":[makeQuery(id+"F61.opExtrude","CAP_FACE",FACE,{"disambiguationData":[OSD([sQuery(id+"F60.wireOp",EDGE,"E88.bottom"),sQuery(id+"F60.wireOp",EDGE,"E88.top"),sQuery(id+"F60.wireOp",EDGE,"E88.left"),sQuery(id+"F60.wireOp",EDGE,"E88.right")])],"isStart":false})]});
            var sketch = newSketch(context, id + "F62", { "sketchPlane" : qUnion([Q0])});
            skLineSegment(sketch, "E89.bottom", {"start": v(8900, 3300) * mm, "end": v(10500, 3300) * mm});
            skLineSegment(sketch, "E89.top", {"start": v(8900, 2800) * mm, "end": v(10500, 2800) * mm});
            skLineSegment(sketch, "E89.left", {"start": v(8900, 3300) * mm, "end": v(8900, 2800) * mm});
            skLineSegment(sketch, "E89.right", {"start": v(10500, 3300) * mm, "end": v(10500, 2800) * mm});
            skSolve(sketch);
        }
        {
            var Q0;
            Q0=qSketchRegion(id+"F62",true);
            extrude(context, id + "F63", {"entities" : qUnion([Q0]), "operationType" : NewBodyOperationType.REMOVE, "oppositeDirection" : true, "depth" : 300 * mm, "offsetDistance" : 25 * mm});
        }
        {
            var Q0;
            Q0=makeQuery(id+"F63.boolean.opBoolean","MERGE",FACE,{"derivedFrom":[makeQuery(id+"F31.opExtrude","CAP_FACE",FACE,{"disambiguationData":[OSD([sQuery(id+"F30.wireOp",EDGE,"E69"),sQuery(id+"F30.wireOp",EDGE,"E70"),sQuery(id+"F30.wireOp",EDGE,"E71"),sQuery(id+"F30.wireOp",EDGE,"E72"),sQuery(id+"F30.wireOp",EDGE,"E73")])],"isStart":false})],"fromTools":[makeQuery(id+"F63.opExtrude","CAP_FACE",FACE,{"disambiguationData":[OSD([sQuery(id+"F62.wireOp",EDGE,"E89.bottom"),sQuery(id+"F62.wireOp",EDGE,"E89.top"),sQuery(id+"F62.wireOp",EDGE,"E89.left"),sQuery(id+"F62.wireOp",EDGE,"E89.right")])],"isStart":false})]});
            var sketch = newSketch(context, id + "F64", { "sketchPlane" : qUnion([Q0])});
            skLineSegment(sketch, "E90.bottom", {"start": v(9200, 3300) * mm, "end": v(10500, 3300) * mm});
            skLineSegment(sketch, "E90.top", {"start": v(9200, 2800) * mm, "end": v(10500, 2800) * mm});
            skLineSegment(sketch, "E90.left", {"start": v(9200, 3300) * mm, "end": v(9200, 2800) * mm});
            skLineSegment(sketch, "E90.right", {"start": v(10500, 3300) * mm, "end": v(10500, 2800) * mm});
            skSolve(sketch);
        }
        {
            var Q0;
            Q0=qSketchRegion(id+"F64",true);
            extrude(context, id + "F65", {"entities" : qUnion([Q0]), "operationType" : NewBodyOperationType.REMOVE, "oppositeDirection" : true, "depth" : 300 * mm, "offsetDistance" : 25 * mm});
        }
        {
            var Q0;
            Q0=makeQuery(id+"F65.boolean.opBoolean","MERGE",FACE,{"derivedFrom":[makeQuery(id+"F29.opExtrude","CAP_FACE",FACE,{"disambiguationData":[OSD([sQuery(id+"F28.wireOp",EDGE,"E65"),sQuery(id+"F28.wireOp",EDGE,"E66"),sQuery(id+"F28.wireOp",EDGE,"E67"),sQuery(id+"F28.wireOp",EDGE,"E68")])],"isStart":false})],"fromTools":[makeQuery(id+"F65.opExtrude","CAP_FACE",FACE,{"disambiguationData":[OSD([sQuery(id+"F64.wireOp",EDGE,"E90.bottom"),sQuery(id+"F64.wireOp",EDGE,"E90.top"),sQuery(id+"F64.wireOp",EDGE,"E90.left"),sQuery(id+"F64.wireOp",EDGE,"E90.right")])],"isStart":false})]});
            var sketch = newSketch(context, id + "F66", { "sketchPlane" : qUnion([Q0])});
            skLineSegment(sketch, "E91.bottom", {"start": v(9500, 3300) * mm, "end": v(10500, 3300) * mm});
            skLineSegment(sketch, "E91.top", {"start": v(9500, 2800) * mm, "end": v(10500, 2800) * mm});
            skLineSegment(sketch, "E91.left", {"start": v(9500, 3300) * mm, "end": v(9500, 2800) * mm});
            skLineSegment(sketch, "E91.right", {"start": v(10500, 3300) * mm, "end": v(10500, 2800) * mm});
            skSolve(sketch);
        }
        {
            var Q0;
            Q0=qSketchRegion(id+"F66",true);
            extrude(context, id + "F67", {"entities" : qUnion([Q0]), "operationType" : NewBodyOperationType.REMOVE, "oppositeDirection" : true, "depth" : 300 * mm, "offsetDistance" : 25 * mm});
        }
        {
            var Q0;
            Q0=makeQuery(id+"F3.boolean.opBoolean","MERGE",FACE,{"derivedFrom":[makeQuery(id+"F1.opExtrude","SWEPT_FACE",FACE,{"disambiguationData":[OSD([sQuery(id+"F0.wireOp",EDGE,"E0.left")])]}),makeQuery(id+"F3.opExtrude","SWEPT_FACE",FACE,{"disambiguationData":[OSD([sQuery(id+"F2.wireOp",EDGE,"E5")])]})]});
            var sketch = newSketch(context, id + "F68", { "sketchPlane" : qUnion([Q0])});
            skLineSegment(sketch, "E92", {"start": v(3500, 2700) * mm, "end": v(7000, 2700) * mm});
            skLineSegment(sketch, "E93", {"start": v(7000, 2700) * mm, "end": v(7000, 4800) * mm});
            skLineSegment(sketch, "E94", {"start": v(7000, 4800) * mm, "end": v(3500, 4800) * mm});
            skLineSegment(sketch, "E95", {"start": v(3500, 4800) * mm, "end": v(3500, 2700) * mm});
            skSolve(sketch);
        }
        {
            var Q0;
            Q0 = qSketchRegion(id + "F68", true);
            extrude(context, id + "F69", {"entities" : qUnion([Q0]), "operationType" : NewBodyOperationType.ADD, "depth" : 1500 * mm, "offsetDistance" : 25 * mm});
        }
        {
            var Q0;
            Q0=makeQuery(id+"F69.opExtrude","CAP_FACE",FACE,{"disambiguationData":[OSD([sQuery(id+"F68.wireOp",EDGE,"E92"),sQuery(id+"F68.wireOp",EDGE,"E93"),sQuery(id+"F68.wireOp",EDGE,"E94"),sQuery(id+"F68.wireOp",EDGE,"E95")])],"isStart":false});
            var sketch = newSketch(context, id + "F70", { "sketchPlane" : qUnion([Q0])});
            skSolve(sketch);
        }
        {
            var Q0;
            Q0=makeQuery(id+"F70.imprint","IMPRINT",FACE,{"disambiguationData":[TD([[makeQuery(id+"F70.imprint","IMPRINT",EDGE,{"derivedFrom":makeQuery(id+"F69.opExtrude","CAP_EDGE",EDGE,{"disambiguationData":[OSD([sQuery(id+"F68.wireOp",EDGE,"E92")])],"isStart":false})}),1.0]])]});
            var sketch = newSketch(context, id + "F71", { "sketchPlane" : qUnion([Q0])});
            skLineSegment(sketch, "E96", {"start": v(3505.9, 4802.63) * mm, "end": v(3655.9, 4802.63) * mm});
            skLineSegment(sketch, "E97", {"start": v(3655.9, 4802.63) * mm, "end": v(3655.9, 3702.63) * mm});
            skLineSegment(sketch, "E98", {"start": v(3655.9, 3702.63) * mm, "end": v(6855.9, 3702.63) * mm});
            skLineSegment(sketch, "E99", {"start": v(6855.9, 3702.63) * mm, "end": v(6855.9, 4802.63) * mm});
            skLineSegment(sketch, "E100", {"start": v(6855.9, 4802.63) * mm, "end": v(3655.9, 4802.63) * mm});
            skSolve(sketch);
        }
        {
            var Q0;
            Q0 = qSketchRegion(id + "F71", true);
            extrude(context, id + "F72", {"entities" : qUnion([Q0]), "operationType" : NewBodyOperationType.REMOVE, "oppositeDirection" : true, "depth" : 1500 * mm, "offsetDistance" : 25 * mm});
        }
        {
            var Q0;
            Q0=makeQuery(id+"F69.opExtrude","SWEPT_FACE",FACE,{"disambiguationData":[OSD([sQuery(id+"F68.wireOp",EDGE,"E95")])]});
            var sketch = newSketch(context, id + "F73", { "sketchPlane" : qUnion([Q0])});
            skLineSegment(sketch, "E101", {"start": v(1500, 4800) * mm, "end": v(1350, 4800) * mm});
            skLineSegment(sketch, "E102", {"start": v(1350, 4800) * mm, "end": v(1350, 3700) * mm});
            skLineSegment(sketch, "E103", {"start": v(1350, 3700) * mm, "end": v(0, 3700) * mm});
            skLineSegment(sketch, "E104", {"start": v(0, 3700) * mm, "end": v(0, 4800) * mm});
            skLineSegment(sketch, "E105", {"start": v(0, 4800) * mm, "end": v(1350, 4800) * mm});
            skSolve(sketch);
        }
        {
            var Q0;
            Q0 = qSketchRegion(id + "F73", true);
            extrude(context, id + "F74", {"entities" : qUnion([Q0]), "operationType" : NewBodyOperationType.REMOVE, "oppositeDirection" : true, "depth" : 3500 * mm, "offsetDistance" : 25 * mm});
        }
        {
            var Q0;
            Q0=makeQuery(id+"F74.boolean.opBoolean","COPY",FACE,{"derivedFrom":makeQuery(id+"F74.opExtrude","SWEPT_FACE",FACE,{"disambiguationData":[OSD([sQuery(id+"F73.wireOp",EDGE,"E103")])]})});
            shell(context, id + "F75", {"entities" : qUnion([Q0]), "thickness" : 150 * mm});
        }
    });
